# Revit family: Building-IEC309Boards-GEWISS-68QDIN-DISTRIBUTION-BOARD-10MOD_BLANK
name_source: partatom
category: Apparecchi elettrici
units: mm (PartAtom-declared; Revit-internal decimal feet)

## family parameters
Condiviso = No
Host = Superficie
Mantenere orientamento annotazione = Sì
Punto di calcolo locali = Sì
Quota connettore circolare = Usa diametro
Taglio con vuoti quando caricato = No
Tipo di parte = Normale

## types (1)
- GW68002N - Q-DIN 10M COP.435x220x95 BLIND IP65
    Accordance with Standards = EN 60208 - EN 60670-1 - IEC 60670-24
    Catalogue = BUILDING
    Catalogue Range = 68 QDIN
    Colour = Grey RAL 7035
    Descrizione = Q-DIN 10M COP.435x220x95 BLIND IP65
    Dispersible power A (W) = 16
    Dispersible power B (W) = 42
    EAN code = 8011564744738
    Electrocod = 2242
    Glow Wire Test = 650°C
    Houseable socket = Blank lid
    IDF = 5341b2a5-b902-4f80-ae8c-9d5b282bb473
    IDT = 5251850b-27dc-44a4-affc-d4abd1ca87ad
    IP degree = IP65
    Immagine tipo = GW68002N.jpg
    Installation type = Surface-mounting
    Insulation class = II
    L_Moduli = 190 mm  [stored 0.62336 ft]
    Modello = GW68002N
    N_Moduli = 10 mm  [stored 0.0328084 ft]
    No. of modules EN 50022 = 10
    No. of provided blank lids = -
    Operating temperature: = -25 +40 °C
    POMELLO = bianco
    PRESA = rosso
    Produttore = GEWISS S.p.A.
    Prospetto di default = 1219 mm
    SEO = Board
    STRUTTURA = RAL - 7035
    STRUTTURA ALTA = Poche
    Shock resistance = IK09
    Spostamento_S = 1000 mm  [stored 3.28084 ft]
    Technical sheet = https://www.gewiss.com
    Thermo-pressure with ball = 70
    URL = https://www.gewiss.com
    VETRO = Vetro
    Version file RFA = 21.5
    Version type = Empty

note: source unit labels omitted for Thermo-pressure with ball — the stored unit's dimension contradicts the parameter name (converter mislabeling)

note: [stored X ft] marks values corroborated as IEEE doubles in the binary element streams (Revit-internal decimal feet)

## geometry (parser evidence)
native form markers: Sweep x3
no freeform markers — native parametric forms only
